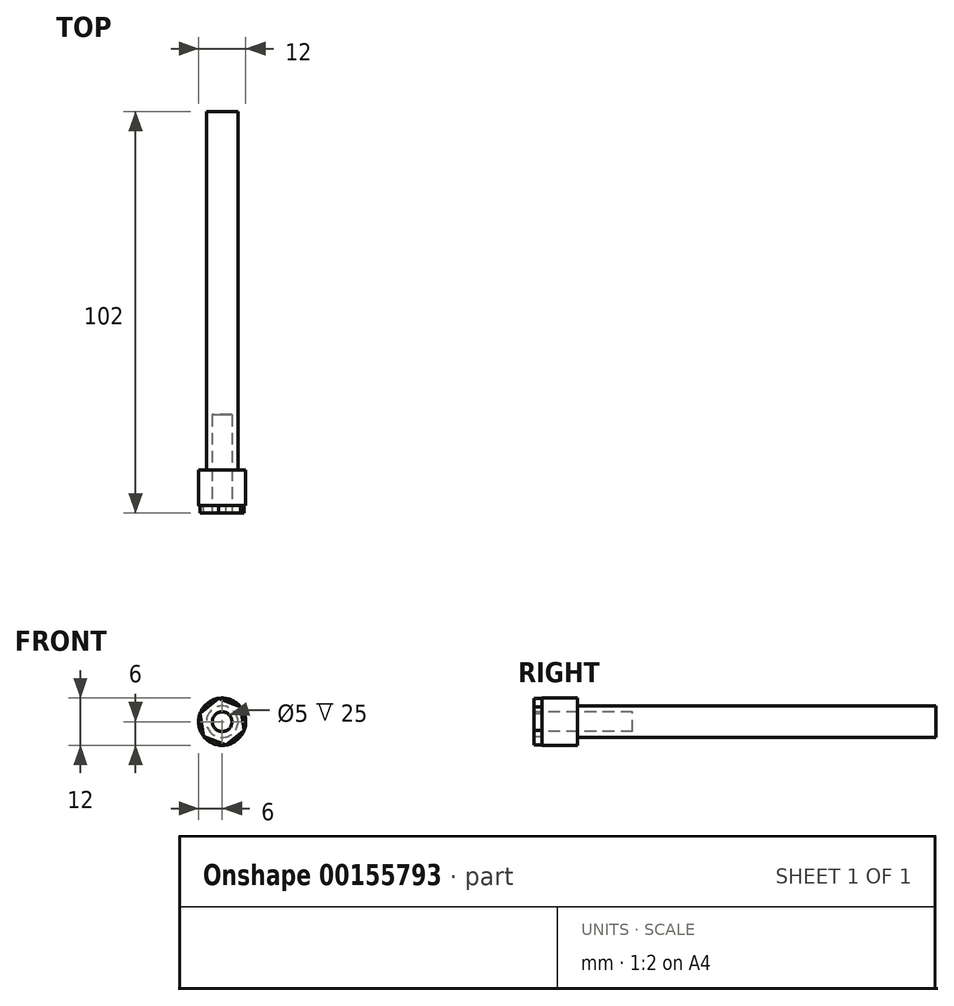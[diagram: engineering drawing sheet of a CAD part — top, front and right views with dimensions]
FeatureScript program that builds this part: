
annotation { "Feature Type Name" : "Feature", "Feature Type Description" : "" }
export const myFeature = defineFeature(function(context is Context, id is Id, definition is map)
    precondition{}
    {
        {
            var Q0;
            Q0=qCreatedBy(makeId("Front.planeOp"),FACE);
            var sketch = newSketch(context, id + "F0", { "sketchPlane" : qUnion([Q0])});
            skLineSegment(sketch, "E0", {"start": v(-23.03, 0) * mm, "end": v(26.95, 0) * mm, "construction": true});
            skLineSegment(sketch, "E1", {"start": v(0, 23.84) * mm, "end": v(0, -25.66) * mm, "construction": true});
            skCircle(sketch, "E2", {"center": v(0, 0) * mm, "radius": 6 * mm});
            skSolve(sketch);
        }
        {
            var Q0;
            Q0 = qSketchRegion(id + "F0", true);
            extrude(context, id + "F1", {"entities" : qUnion([Q0]), "depth" : 75 * mm, "hasSecondDirection" : true, "secondDirectionOppositeDirection" : true, "secondDirectionDepth" : 25 * mm});
        }
        {
            var Q0;
            Q0=makeQuery(id+"F1.opExtrude","CAP_FACE",FACE,{"disambiguationData":[OSD([sQuery(id+"F0.wireOp",EDGE,"E2")])],"isStart":false});
            var sketch = newSketch(context, id + "F2", { "sketchPlane" : qUnion([Q0])});
            skCircle(sketch, "E3.cCircle", {"center": v(0, 0) * mm, "radius": 5.2 * mm, "construction": true});
            skLineSegment(sketch, "E3.0", {"start": v(4.67, 3.77) * mm, "end": v(5.6, -2.16) * mm});
            skLineSegment(sketch, "E3.1", {"start": v(5.6, -2.16) * mm, "end": v(0.93, -5.93) * mm});
            skLineSegment(sketch, "E3.2", {"start": v(0.93, -5.93) * mm, "end": v(-4.67, -3.77) * mm});
            skLineSegment(sketch, "E3.3", {"start": v(-4.67, -3.77) * mm, "end": v(-5.6, 2.16) * mm});
            skLineSegment(sketch, "E3.4", {"start": v(-5.6, 2.16) * mm, "end": v(-0.93, 5.93) * mm});
            skLineSegment(sketch, "E3.5", {"start": v(-0.93, 5.93) * mm, "end": v(4.67, 3.77) * mm});
            skPoint(sketch, "E3.0.midPoint", {"position": v(5.13, 0.8) * mm});
            skSolve(sketch);
        }
        {
            var Q0;
            Q0 = qSketchRegion(id + "F2", true);
            extrude(context, id + "F3", {"entities" : qUnion([Q0]), "operationType" : NewBodyOperationType.ADD, "depth" : 2 * mm});
        }
        {
            var Q0;
            Q0=makeQuery(id+"F3.opExtrude","CAP_FACE",FACE,{"disambiguationData":[OSD([sQuery(id+"F2.wireOp",EDGE,"E3.0"),sQuery(id+"F2.wireOp",EDGE,"E3.1"),sQuery(id+"F2.wireOp",EDGE,"E3.2"),sQuery(id+"F2.wireOp",EDGE,"E3.3"),sQuery(id+"F2.wireOp",EDGE,"E3.4"),sQuery(id+"F2.wireOp",EDGE,"E3.5")])],"isStart":false});
            var sketch = newSketch(context, id + "F4", { "sketchPlane" : qUnion([Q0])});
            skCircle(sketch, "E4", {"center": v(0, 0) * mm, "radius": 2.5 * mm});
            skSolve(sketch);
        }
        {
            var Q0;
            Q0 = qSketchRegion(id + "F4", true);
            extrude(context, id + "F5", {"entities" : qUnion([Q0]), "operationType" : NewBodyOperationType.REMOVE, "oppositeDirection" : true, "depth" : 25 * mm});
        }
        {
            var Q0;
            Q0=makeQuery(id+"F1.opExtrude","CAP_FACE",FACE,{"disambiguationData":[OSD([sQuery(id+"F0.wireOp",EDGE,"E2")])],"isStart":true});
            var sketch = newSketch(context, id + "F6", { "sketchPlane" : qUnion([Q0])});
            skCircle(sketch, "E5", {"center": v(0, 0) * mm, "radius": 4 * mm});
            skCircle(sketch, "E6", {"center": v(0, 0) * mm, "radius": 6 * mm});
            skSolve(sketch);
        }
        {
            var Q0;
            Q0 = qSketchRegion(id + "F6", true);
            extrude(context, id + "F7", {"entities" : qUnion([Q0]), "operationType" : NewBodyOperationType.REMOVE, "oppositeDirection" : true, "depth" : 91 * mm, "offsetDistance" : 25 * mm});
        }
    });
